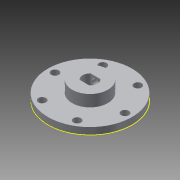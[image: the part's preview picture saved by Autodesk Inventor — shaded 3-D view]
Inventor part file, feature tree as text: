
AUTODESK INVENTOR PART (.ipt)
format: ipt  version: 2013 (Build 170138000, 138)  size: 133,632 bytes
history: native  units: in
note: dims shown in document units (in); Inventor stores cm internally (conversion verified against a paired STEP export)
features: sketch x4, extrude x3
ambient origin geometry x8: Origin, YZ Plane, XZ Plane, XY Plane, X Axis, Y Axis, Z Axis, Center Point
bodies: Solid1 (feature_tree)
feature tree (7):
  extrude  "Extrusion1"  Depth=1.875in
  extrude  "Extrusion2"  Depth=2.3622in TaperAngle=360.0deg
  extrude  "Extrusion3"  Depth=0.2955in
  sketch  "Sketch4"  dims[d9=0.1478in d10=0.18in d11=0.0in d12=0.958in d14=0.31in d15=0.0in d16=0.19in d17=0.15in d18=0.1299in d19=0.31in d20=0.0in]
  sketch  "Sketch1"  dims[d0=2.25in d1=1.875in]
  sketch  "Sketch2"  dims[d2=0.204in d3=2.3622in d5=360.0deg]
  sketch  "Sketch3"  dims[d7=0.3935in d8=0.2955in]
